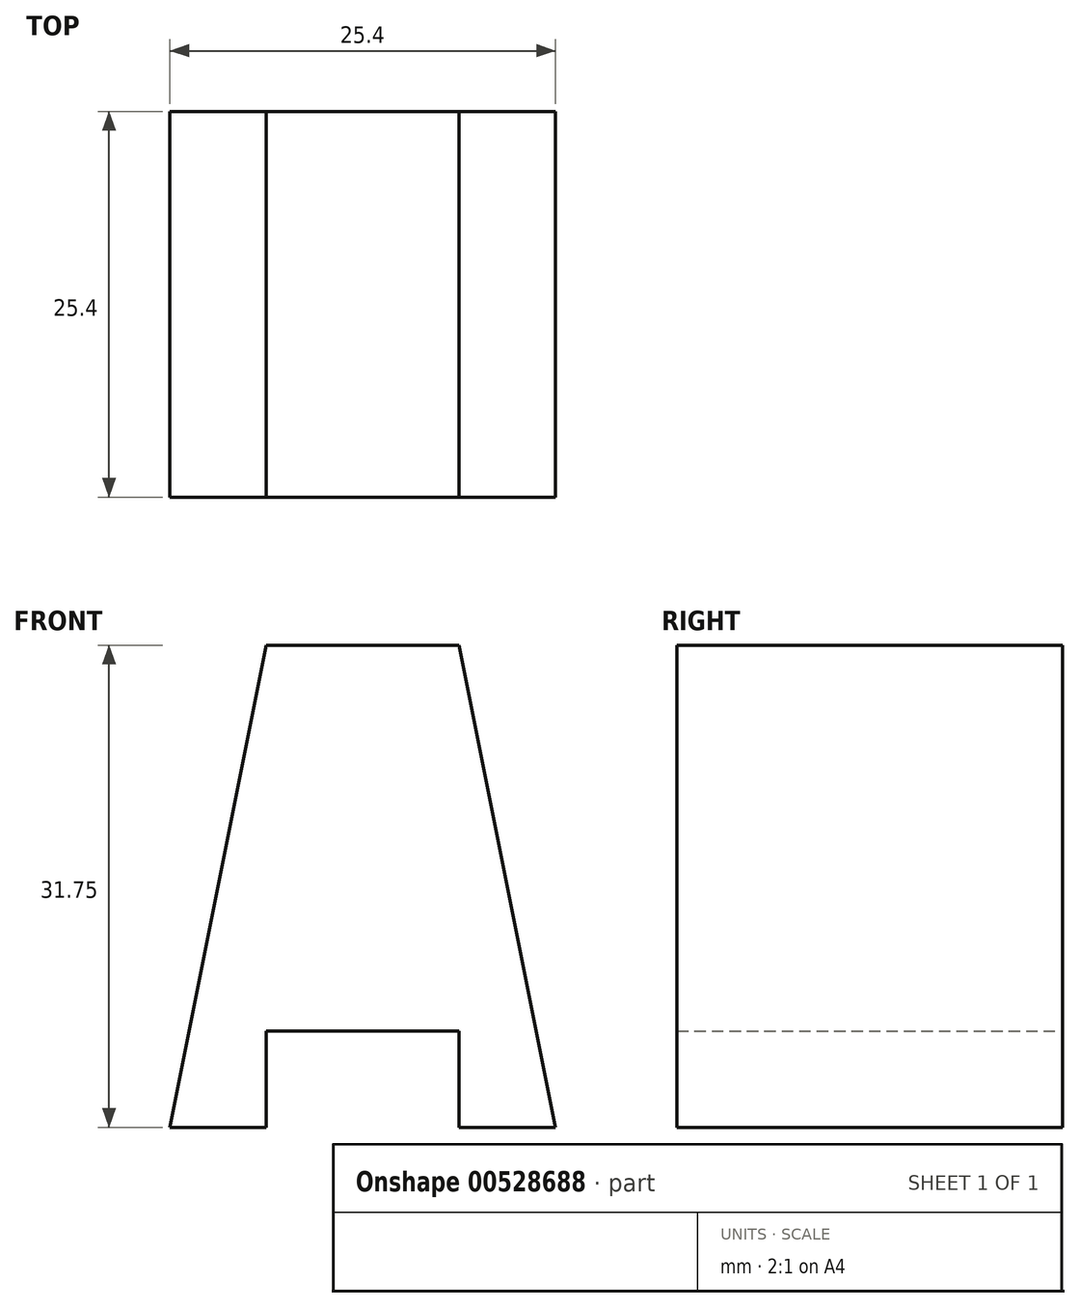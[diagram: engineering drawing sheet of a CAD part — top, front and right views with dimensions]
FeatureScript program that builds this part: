
annotation { "Feature Type Name" : "Feature", "Feature Type Description" : "" }
export const myFeature = defineFeature(function(context is Context, id is Id, definition is map)
    precondition{}
    {
        {
            var Q0;
            Q0=qCreatedBy(makeId("Front.planeOp"),FACE);
            var sketch = newSketch(context, id + "F0", { "sketchPlane" : qUnion([Q0])});
            skLineSegment(sketch, "E0", {"start": v(6.35, 0) * mm, "end": v(12.7, 0) * mm});
            skLineSegment(sketch, "E1", {"start": v(-6.35, 0) * mm, "end": v(-12.7, 0) * mm});
            skLineSegment(sketch, "E2", {"start": v(-6.35, 31.75) * mm, "end": v(-12.7, 0) * mm});
            skLineSegment(sketch, "E3", {"start": v(6.35, 31.75) * mm, "end": v(12.7, 0) * mm});
            skPoint(sketch, "E4.start.orphan", {"position": v(0, 31.75) * mm});
            skLineSegment(sketch, "E5", {"start": v(-6.35, 31.75) * mm, "end": v(6.35, 31.75) * mm});
            skLineSegment(sketch, "E6", {"start": v(-6.35, 0) * mm, "end": v(-6.35, 6.35) * mm});
            skLineSegment(sketch, "E7", {"start": v(-6.35, 6.35) * mm, "end": v(6.35, 6.35) * mm});
            skLineSegment(sketch, "E8", {"start": v(6.35, 6.35) * mm, "end": v(6.35, 0) * mm});
            skPoint(sketch, "E9.orphan", {"position": v(0, 0) * mm});
            skSolve(sketch);
        }
        {
            var Q0;
            Q0=makeQuery(id+"F0.imprint","IMPRINT",FACE,{"disambiguationData":[TD([[makeQuery(id+"F0.imprint","IMPRINT",EDGE,{"derivedFrom":sQuery(id+"F0.wireOp",EDGE,"E0")}),1.0]])]});
            extrude(context, id + "F1", {"entities" : qUnion([Q0]), "depth" : 25.4 * mm, "offsetDistance" : 25.4 * mm});
        }
    });
